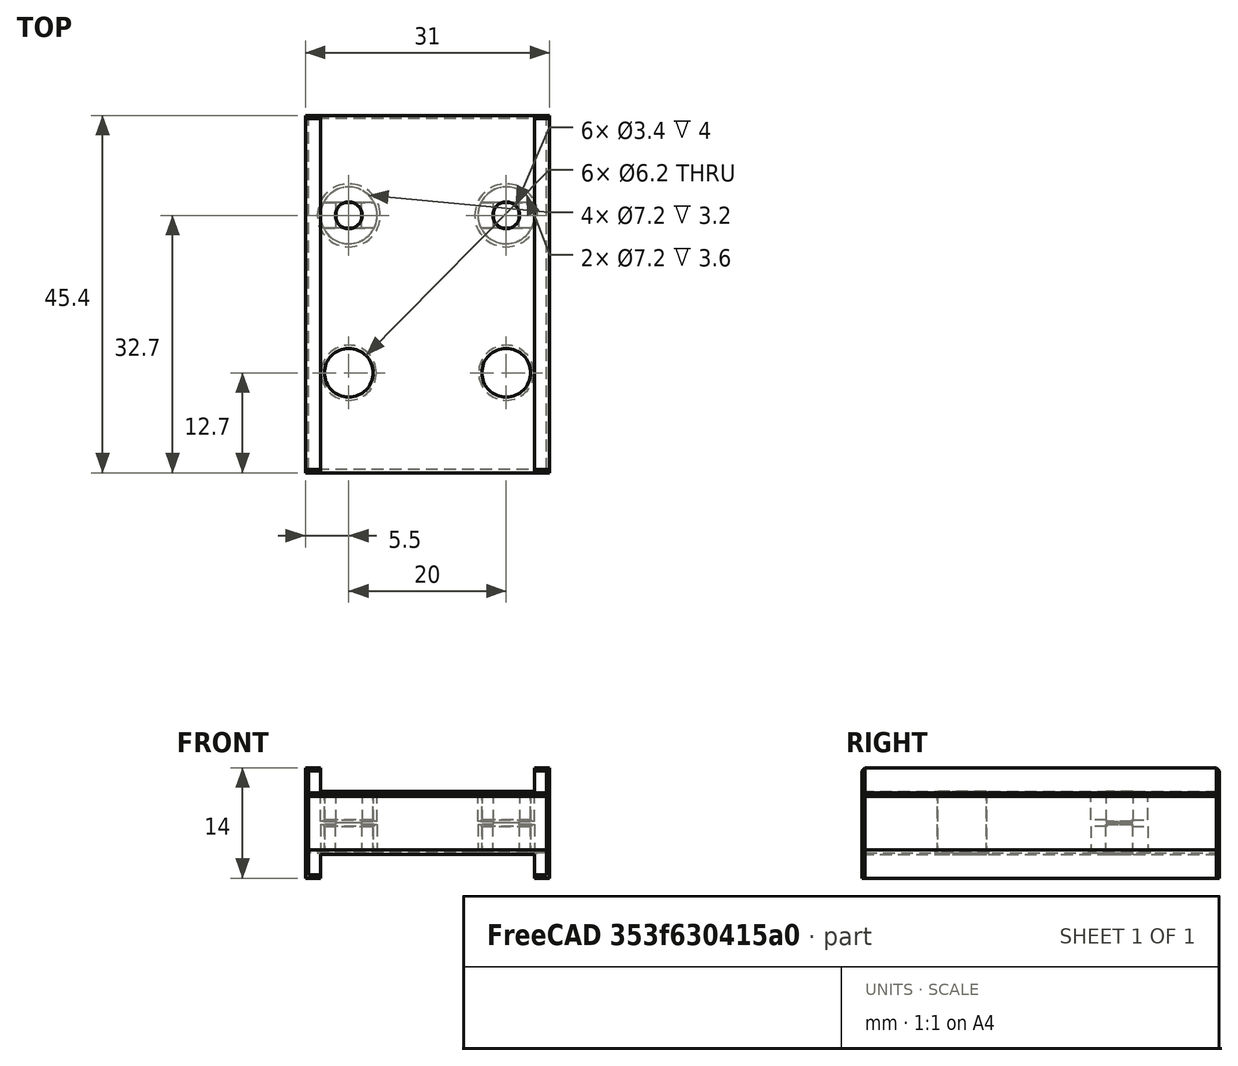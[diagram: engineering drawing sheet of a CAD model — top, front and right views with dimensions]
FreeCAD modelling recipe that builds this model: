
FCSTD DOCUMENT  (FreeCAD 0.18R14555 (Git shallow))
Label: 12h-block-8mm-raiser
License: All rights reserved
LicenseURL: http://en.wikipedia.org/wiki/All_rights_reserved
objects: Part::Box×7, Part::Cylinder×7, Part::MultiFuse×5, Part::Cut×4, Part::Feature×3, Part::MultiCommon×1, Part::Chamfer×1
note: 28 computed .brp shape members not serialized (recipe doc carries the construction recipe); baked Part::Feature solids carry a one-line shape summary decoded from their .brp

FEATURE [Part::Box] Box  label="Cube"
  AttacherType = Attacher::AttachEngine3D
  Height = 7.8
  Length = 31
  Placement = pos=(-15.5,0,0) rot=(0,0,1;0rad)
  Width = 45.4
FEATURE [Part::Box] Box001  label="Cube001"
  AttacherType = Attacher::AttachEngine3D
  Height = 3
  Length = 1.9
  Placement = pos=(-15.5,0,-3) rot=(0,0,1;0rad)
  Width = 45.4
FEATURE [Part::Box] Box002  label="Cube002"
  AttacherType = Attacher::AttachEngine3D
  Height = 3
  Length = 1.9
  Placement = pos=(13.6,0,-3) rot=(0,0,1;0rad)
  Width = 45.4
FEATURE [Part::Cylinder] Cylinder
  Angle = 360
  AttacherType = Attacher::AttachEngine3D
  Height = 10
  Placement = pos=(10,12.7,0) rot=(0,0,1;0rad)
  Radius = 3.1
FEATURE [Part::Cylinder] Cylinder001
  Angle = 360
  AttacherType = Attacher::AttachEngine3D
  Height = 4
  Placement = pos=(-10,32.7,4) rot=(0,0,1;0rad)
  Radius = 3.6
FEATURE [Part::Cylinder] Cylinder002
  Angle = 360
  AttacherType = Attacher::AttachEngine3D
  Height = 4
  Placement = pos=(10,32.7,4) rot=(0,0,1;0rad)
  Radius = 3.6
FEATURE [Part::Cylinder] Cylinder003
  Angle = 360
  AttacherType = Attacher::AttachEngine3D
  Height = 10
  Placement = pos=(-10,12.7,0) rot=(0,0,1;0rad)
  Radius = 3.1
FEATURE [Part::Cut] Cut
  Base = -> Box
  Tool = -> Cylinder003
FEATURE [Part::Cut] Cut001
  Base = -> Cut
  Tool = -> Cylinder
FEATURE [Part::Cylinder] Cylinder004
  Angle = 360
  AttacherType = Attacher::AttachEngine3D
  Height = 10
  Placement = pos=(-10,32.7,0) rot=(0,0,1;0rad)
  Radius = 1.7
FEATURE [Part::Cylinder] Cylinder005
  Angle = 360
  AttacherType = Attacher::AttachEngine3D
  Height = 10
  Placement = pos=(10,32.7,0) rot=(0,0,1;0rad)
  Radius = 1.7
FEATURE [Part::MultiFuse] Fusion
  Shapes = -> [Cylinder004,Cylinder005]
FEATURE [Part::Cut] Cut002
  Base = -> Cut001
  Tool = -> Fusion
FEATURE [Part::MultiFuse] Fusion001
  Shapes = -> [Cylinder002,Cylinder001]
FEATURE [Part::Cut] Cut003
  Base = -> Cut002
  Tool = -> Fusion001
FEATURE [Part::MultiFuse] Fusion002
  Shapes = -> [Cut003,Box002,Box001]
FEATURE [Part::Cylinder] Cylinder006
  Angle = 360
  AttacherType = Attacher::AttachEngine3D
  Height = 10
  Radius = 3.7
FEATURE [Part::Box] Box003  label="Cube003"
  AttacherType = Attacher::AttachEngine3D
  Height = 0.4
  Length = 10
  Placement = pos=(-5,1.6,0) rot=(0,0,1;0rad)
  Width = 10
FEATURE [Part::Box] Box004  label="Cube004"
  AttacherType = Attacher::AttachEngine3D
  Height = 0.4
  Length = 10
  Placement = pos=(-5,-11.6,0) rot=(0,0,1;0rad)
  Width = 10
FEATURE [Part::Box] Box005  label="Cube005"
  AttacherType = Attacher::AttachEngine3D
  Height = 0.2
  Length = 10
  Placement = pos=(-11.6,-5,0) rot=(0,0,1;0rad)
  Width = 10
FEATURE [Part::Box] Box006  label="Cube006"
  AttacherType = Attacher::AttachEngine3D
  Height = 0.2
  Length = 10
  Placement = pos=(1.6,-5,0) rot=(0,0,1;0rad)
  Width = 10
FEATURE [Part::MultiFuse] Fusion003
  Shapes = -> [Box004,Box003,Box006,Box005]
FEATURE [Part::MultiCommon] Common
  Placement = pos=(-10,32.7,4) rot=(0,0,1;0rad)
  Shapes = -> [Cylinder006,Fusion003]
FEATURE [Part::Feature] Common001
  Placement = pos=(10,32.7,4) rot=(0,0,1;0rad)
  shape: bbox 7.4 x 7.4 x 0.4 mm, 17 faces (baked)
FEATURE [Part::MultiFuse] Fusion004
  Shapes = -> [Common001,Common,Fusion002]
FEATURE [Part::Feature] Fusion004001  label="Fusion005"
  shape: bbox 31 x 45.4 x 10.8 mm, 48 faces (baked)
FEATURE [Part::Chamfer] Chamfer
  Base = -> Fusion004001
  Edges = 16 edges r=0.4: [Edge25,Edge42,Edge43,Edge44,Edge45,Edge46,Edge47,Edge48,Edge108,Edge109,Edge110,Edge112,Edge119,Edge120,Edge121,Edge122]
FEATURE [Part::Feature] Chamfer001
  Placement = pos=(-1e-15,0,8) rot=(0,1,0;3.14159rad)
  shape: bbox 31 x 45.4 x 10.8 mm, 68 faces (baked)
